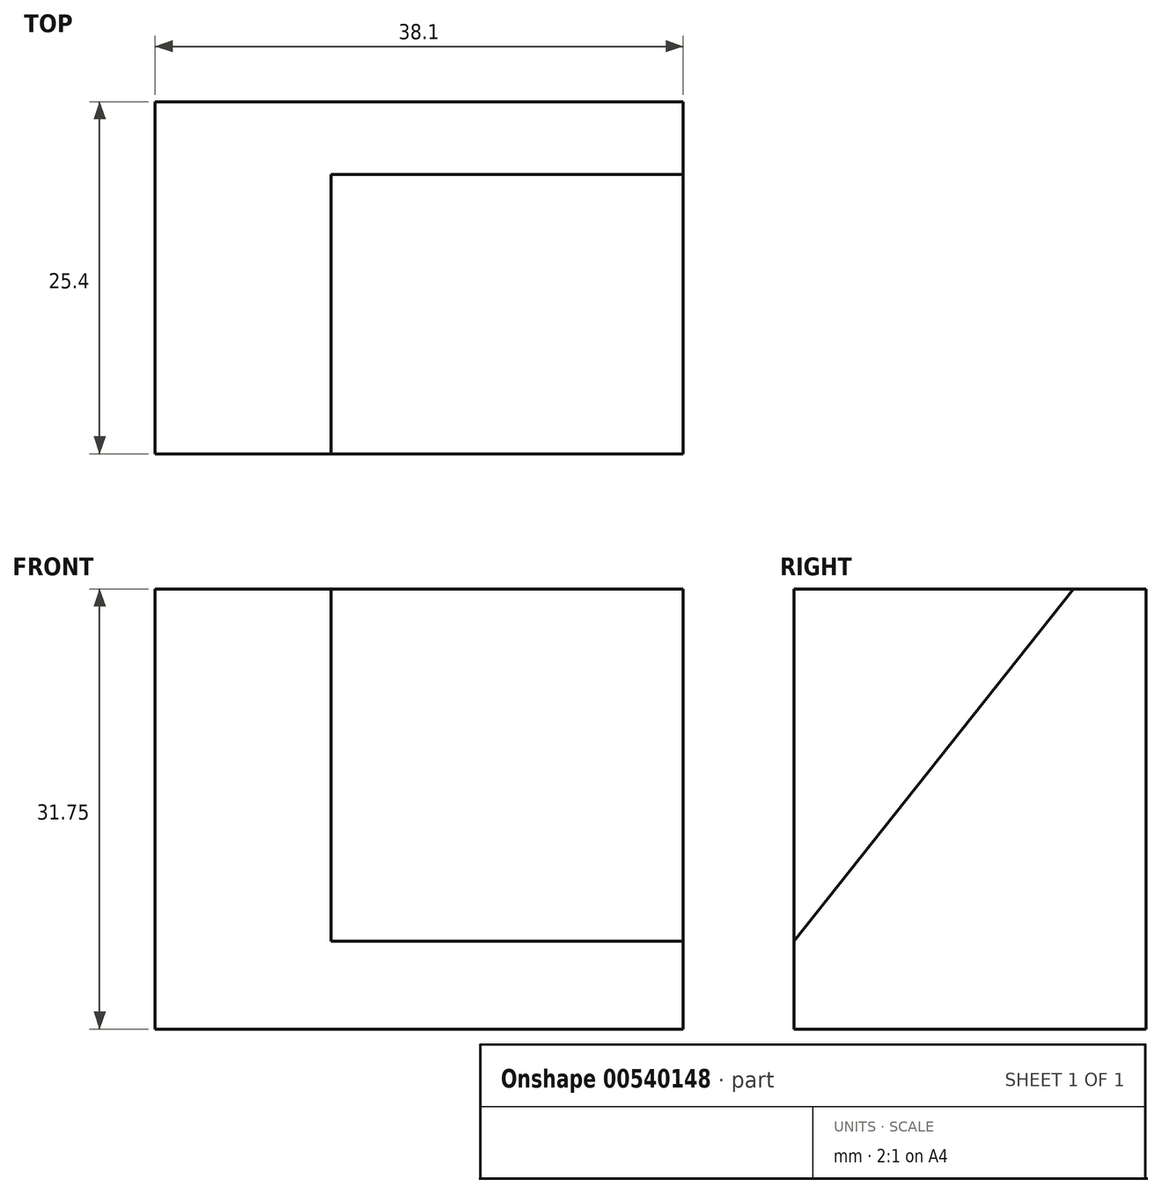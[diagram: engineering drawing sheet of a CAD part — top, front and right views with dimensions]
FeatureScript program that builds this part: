
annotation { "Feature Type Name" : "Feature", "Feature Type Description" : "" }
export const myFeature = defineFeature(function(context is Context, id is Id, definition is map)
    precondition{}
    {
        {
            var Q0;
            Q0=qCreatedBy(makeId("Right.planeOp"),FACE);
            var sketch = newSketch(context, id + "F0", { "sketchPlane" : qUnion([Q0])});
            skLineSegment(sketch, "E0", {"start": v(0, 0) * mm, "end": v(-25.4, 0) * mm});
            skLineSegment(sketch, "E1", {"start": v(-25.4, 0) * mm, "end": v(-25.4, 31.75) * mm});
            skLineSegment(sketch, "E2", {"start": v(-25.4, 31.75) * mm, "end": v(0, 31.75) * mm});
            skLineSegment(sketch, "E3", {"start": v(0, 31.75) * mm, "end": v(0, 0) * mm});
            skSolve(sketch);
        }
        {
            var Q0;
            Q0 = qSketchRegion(id + "F0", true);
            extrude(context, id + "F1", {"entities" : qUnion([Q0]), "depth" : 12.7 * mm, "offsetDistance" : 25.4 * mm});
        }
        {
            var Q0;
            Q0=makeQuery(id+"F1.opExtrude","CAP_FACE",FACE,{"disambiguationData":[OSD([sQuery(id+"F0.wireOp",EDGE,"E0"),sQuery(id+"F0.wireOp",EDGE,"E1"),sQuery(id+"F0.wireOp",EDGE,"E2"),sQuery(id+"F0.wireOp",EDGE,"E3")])],"isStart":false});
            var sketch = newSketch(context, id + "F2", { "sketchPlane" : qUnion([Q0])});
            skLineSegment(sketch, "E4", {"start": v(0, 31.75) * mm, "end": v(-5.26, 31.75) * mm});
            skLineSegment(sketch, "E5", {"start": v(0, 31.75) * mm, "end": v(0, 0) * mm});
            skLineSegment(sketch, "E6", {"start": v(0, 0) * mm, "end": v(-25.4, 0) * mm});
            skLineSegment(sketch, "E7", {"start": v(-25.4, 0) * mm, "end": v(-25.4, 6.35) * mm});
            skLineSegment(sketch, "E8", {"start": v(-5.26, 31.75) * mm, "end": v(-25.4, 6.35) * mm});
            skSolve(sketch);
        }
        {
            var Q0;
            Q0 = qSketchRegion(id + "F2", true);
            extrude(context, id + "F3", {"entities" : qUnion([Q0]), "operationType" : NewBodyOperationType.ADD, "depth" : 25.4 * mm, "offsetDistance" : 25.4 * mm});
        }
    });
